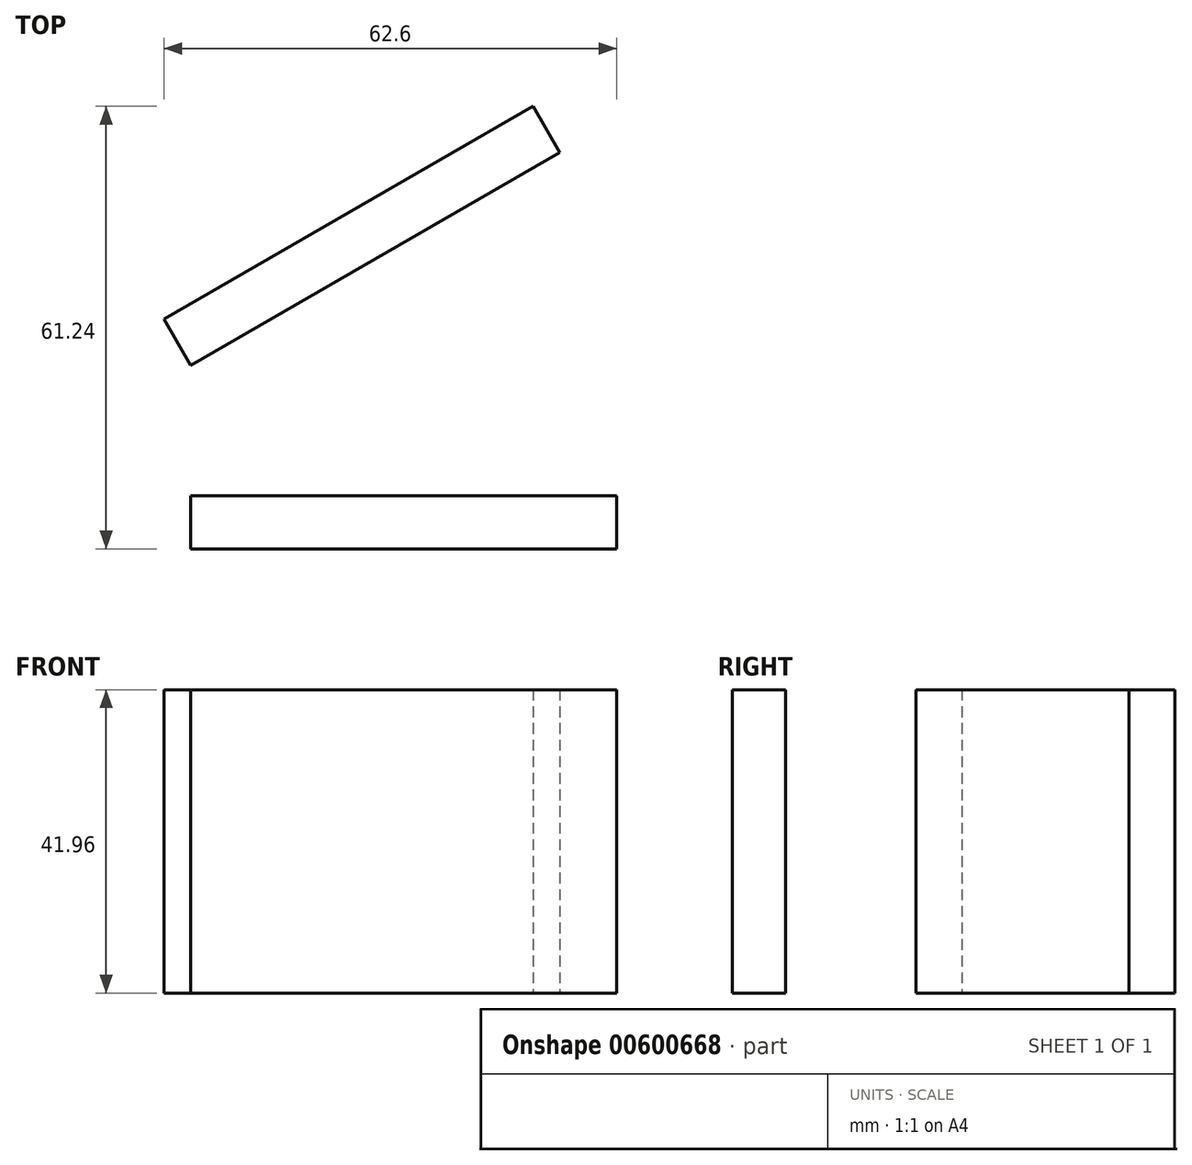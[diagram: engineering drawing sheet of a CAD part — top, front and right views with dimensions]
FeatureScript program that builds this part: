
annotation { "Feature Type Name" : "Feature", "Feature Type Description" : "" }
export const myFeature = defineFeature(function(context is Context, id is Id, definition is map)
    precondition{}
    {
        {
            var Q0;
            Q0=qCreatedBy(makeId("Front.planeOp"),FACE);
            var sketch = newSketch(context, id + "F0", { "sketchPlane" : qUnion([Q0])});
            skLineSegment(sketch, "E0.bottom", {"start": v(-38.24, 47.9) * mm, "end": v(20.68, 47.9) * mm});
            skLineSegment(sketch, "E0.top", {"start": v(-38.24, 5.95) * mm, "end": v(20.68, 5.95) * mm});
            skLineSegment(sketch, "E0.left", {"start": v(-38.24, 47.9) * mm, "end": v(-38.24, 5.95) * mm});
            skLineSegment(sketch, "E0.right", {"start": v(20.68, 47.9) * mm, "end": v(20.68, 5.95) * mm});
            skSolve(sketch);
        }
        {
            var Q0;
            Q0=makeQuery(id+"F0.imprint","IMPRINT",FACE,{"disambiguationData":[TD([[makeQuery(id+"F0.imprint","IMPRINT",EDGE,{"derivedFrom":sQuery(id+"F0.wireOp",EDGE,"E0.bottom")}),-1.0]])]});
            extrude(context, id + "F1", {"entities" : qUnion([Q0]), "depth" : 7.37 * mm, "offsetDistance" : 25.4 * mm});
        }
        {
            var Q0;
            Q0=makeQuery(id+"F1.opExtrude","SWEPT_BODY",BODY,{"disambiguationData":[OSD([sQuery(id+"F0.wireOp",EDGE,"E0.bottom"),sQuery(id+"F0.wireOp",EDGE,"E0.top"),sQuery(id+"F0.wireOp",EDGE,"E0.left"),sQuery(id+"F0.wireOp",EDGE,"E0.right")])]});
            transform(context, id + "F2", {"entities" : qUnion([Q0]), "transformType" : TransformType.TRANSLATION_3D, "dx" : 0 * mm, "dy" : 25.4 * mm, "dz" : 0 * mm, "makeCopy" : true});
        }
        {
            var Q0;
            Q0=makeQuery(id+"F2.opPattern","COPY",BODY,{"derivedFrom":makeQuery(id+"F1.opExtrude","SWEPT_BODY",BODY,{"disambiguationData":[OSD([sQuery(id+"F0.wireOp",EDGE,"E0.bottom"),sQuery(id+"F0.wireOp",EDGE,"E0.top"),sQuery(id+"F0.wireOp",EDGE,"E0.left"),sQuery(id+"F0.wireOp",EDGE,"E0.right")])]}),"instanceName":"1"});
            var Q1;
            Q1=makeQuery(id+"F2.opPattern","COPY",EDGE,{"derivedFrom":makeQuery(id+"F1.opExtrude","CAP_EDGE",EDGE,{"disambiguationData":[OSD([sQuery(id+"F0.wireOp",EDGE,"E0.left")])],"isStart":false}),"instanceName":"1"});
            transform(context, id + "F3", {"entities" : qUnion([Q0]), "transformType" : TransformType.ROTATION, "transformAxis" : qUnion([Q1]), "angle" : 30 * degree, "oppositeDirection" : true, "makeCopy" : false});
        }
    });
